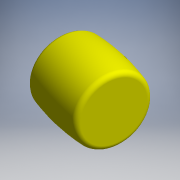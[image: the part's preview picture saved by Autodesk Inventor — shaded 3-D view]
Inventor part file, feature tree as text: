
AUTODESK INVENTOR PART (.ipt)
format: ipt  version: 2017.3 (Build 213256000, 256)  size: 128,000 bytes
history: native  units: mm (DEFAULTED — no unit token found)
features: other x14, revolve x1, sketch x1
ambient origin geometry x8: Origin, YZ Plane, XZ Plane, XY Plane, X Axis, Y Axis, Z Axis, Center Point
bodies: Solid1 (feature_tree)
feature tree (16):
  revolve  "Revolution1"  [1 undecoded]
  other  "NO_GEO_XY"
  other  "NO_GEO_YZ"
  other  "NO_GEO_ZX"
  other  "NO_GEO_X"
  other  "NO_GEO_Y"
  other  "NO_GEO_Z"
  other  "NO_GEO_Center"
  other  "roller1_XY"
  other  "roller1_YZ"
  other  "roller1_ZX"
  other  "roller1_X"
  other  "roller1_Y"
  other  "roller1_Z"
  other  "roller1_Center"
  sketch  "Sketch_2"  dims[d0=360.0deg]
note: 1 required parameter value undecoded (feature->parameter linkage not recoverable at this tier; creation-order binding heuristic only, values carry confidence <= 0.55)
